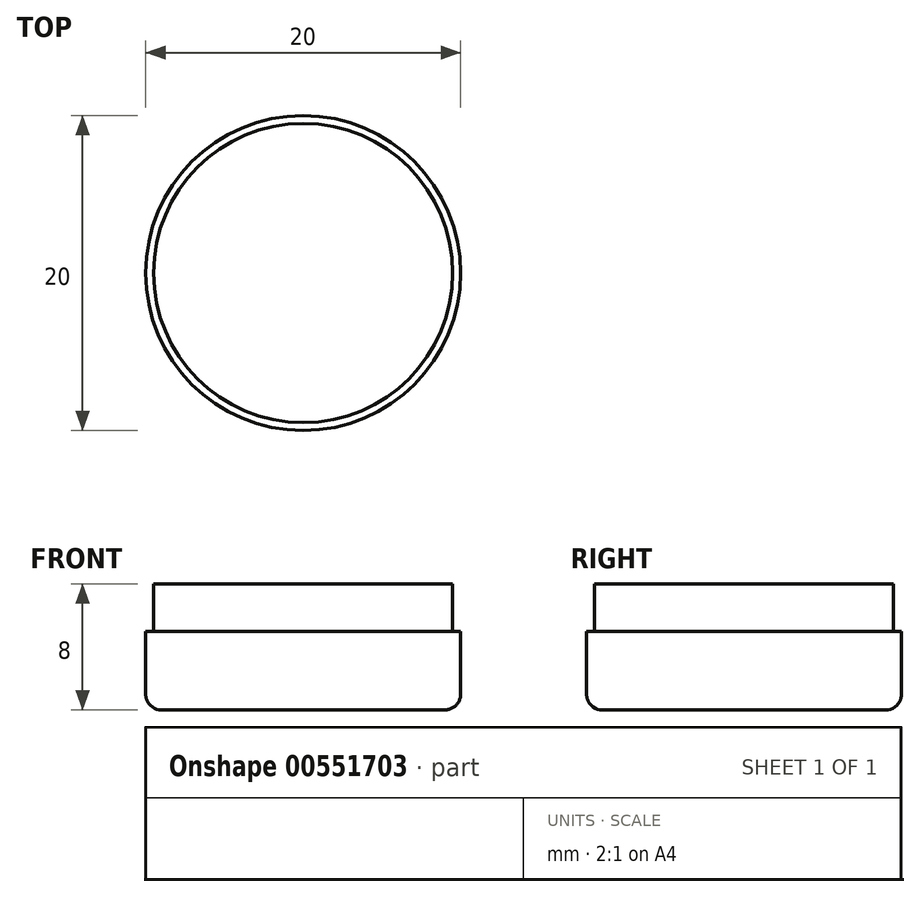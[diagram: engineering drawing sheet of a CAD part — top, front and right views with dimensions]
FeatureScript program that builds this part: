
annotation { "Feature Type Name" : "Feature", "Feature Type Description" : "" }
export const myFeature = defineFeature(function(context is Context, id is Id, definition is map)
    precondition{}
    {
        {
            var Q0;
            Q0=qCreatedBy(makeId("Top.planeOp"),FACE);
            var sketch = newSketch(context, id + "F0", { "sketchPlane" : qUnion([Q0])});
            skCircle(sketch, "E0", {"center": v(0, 0) * mm, "radius": 9.5 * mm});
            skCircle(sketch, "E1", {"center": v(0, 0) * mm, "radius": 10 * mm});
            skSolve(sketch);
        }
        {
            var Q0;
            Q0=makeQuery(id+"F0.imprint","IMPRINT",FACE,{"disambiguationData":[TD([[makeQuery(id+"F0.imprint","IMPRINT",EDGE,{"derivedFrom":sQuery(id+"F0.wireOp",EDGE,"E0")}),1.0]])]});
            extrude(context, id + "F1", {"entities" : qUnion([Q0]), "depth" : 3 * mm, "offsetDistance" : 25 * mm});
        }
        {
            var Q0;
            Q0=makeQuery(id+"F0.imprint","IMPRINT",FACE,{"disambiguationData":[TD([[makeQuery(id+"F0.imprint","IMPRINT",EDGE,{"derivedFrom":sQuery(id+"F0.wireOp",EDGE,"E0")}),1.0]])]});
            var Q1;
            Q1=makeQuery(id+"F0.imprint","IMPRINT",FACE,{"disambiguationData":[TD([[makeQuery(id+"F0.imprint","IMPRINT",EDGE,{"derivedFrom":sQuery(id+"F0.wireOp",EDGE,"E0")}),-1.0]])]});
            extrude(context, id + "F2", {"entities" : qUnion([Q0, Q1]), "operationType" : NewBodyOperationType.ADD, "oppositeDirection" : true, "depth" : 5 * mm, "offsetDistance" : 25 * mm});
        }
        {
            var Q0;
            Q0=makeQuery(id+"F2.opExtrude","CAP_EDGE",EDGE,{"disambiguationData":[OSD([sQuery(id+"F0.wireOp",EDGE,"E1")])],"isStart":false});
            fillet(context, id + "F3", {"entities" : qUnion([Q0]), "radius" : 1 * mm, "tangentPropagation" : true, "allowEdgeOverflow" : false});
        }
    });
